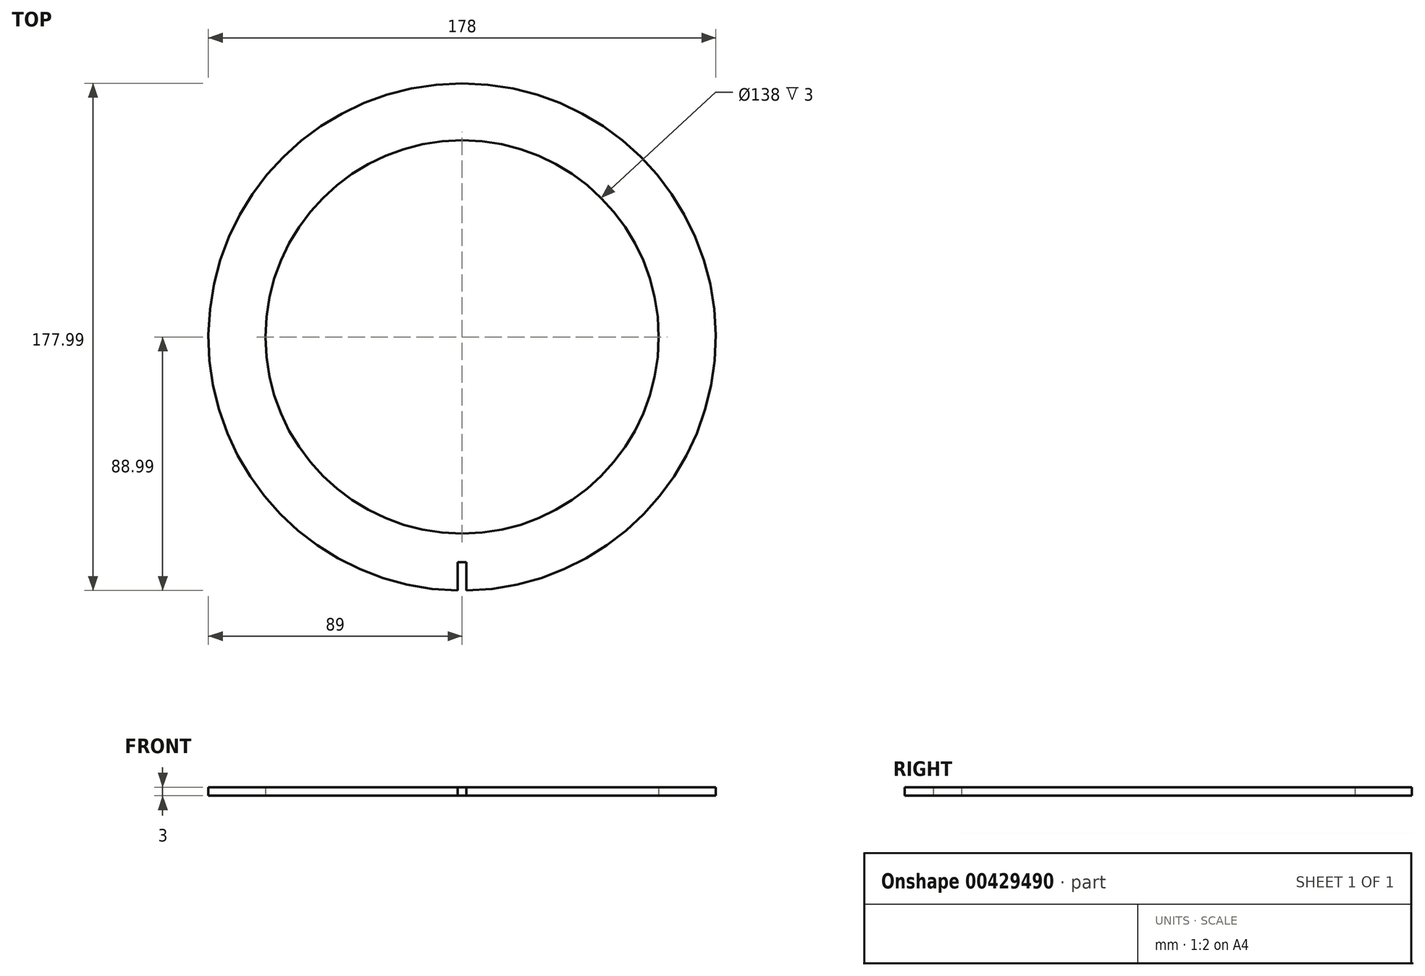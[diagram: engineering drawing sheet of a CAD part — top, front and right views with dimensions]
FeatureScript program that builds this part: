
annotation { "Feature Type Name" : "Feature", "Feature Type Description" : "" }
export const myFeature = defineFeature(function(context is Context, id is Id, definition is map)
    precondition{}
    {
        {
            var Q0;
            Q0=qCreatedBy(makeId("Top.planeOp"),FACE);
            var sketch = newSketch(context, id + "F0", { "sketchPlane" : qUnion([Q0])});
            skCircle(sketch, "E0", {"center": v(0, 0) * mm, "radius": 89 * mm});
            skCircle(sketch, "E1", {"center": v(0, 0) * mm, "radius": 69 * mm});
            skSolve(sketch);
        }
        {
            var Q0;
            Q0=qSketchRegion(id+"F0",true);
            extrude(context, id + "F1", {"entities" : qUnion([Q0]), "depth" : 3 * mm});
        }
        {
            var Q0;
            Q0=qCreatedBy(makeId("Top.planeOp"),FACE);
            var sketch = newSketch(context, id + "F2", { "sketchPlane" : qUnion([Q0])});
            skLineSegment(sketch, "E2", {"start": v(0, 0) * mm, "end": v(0, -89) * mm, "construction": true});
            skLineSegment(sketch, "E3", {"start": v(0, -89) * mm, "end": v(1.5, -89) * mm});
            skLineSegment(sketch, "E4", {"start": v(1.5, -89) * mm, "end": v(1.5, -79) * mm});
            skLineSegment(sketch, "E5", {"start": v(1.5, -79) * mm, "end": v(-1.5, -79) * mm});
            skLineSegment(sketch, "E6", {"start": v(-1.5, -79) * mm, "end": v(-1.5, -89) * mm});
            skLineSegment(sketch, "E7", {"start": v(-1.5, -89) * mm, "end": v(0, -89) * mm});
            skSolve(sketch);
        }
        {
            var Q0;
            Q0=qSketchRegion(id+"F2",true);
            extrude(context, id + "F3", {"entities" : qUnion([Q0]), "operationType" : NewBodyOperationType.REMOVE, "depth" : 25 * mm});
        }
    });
